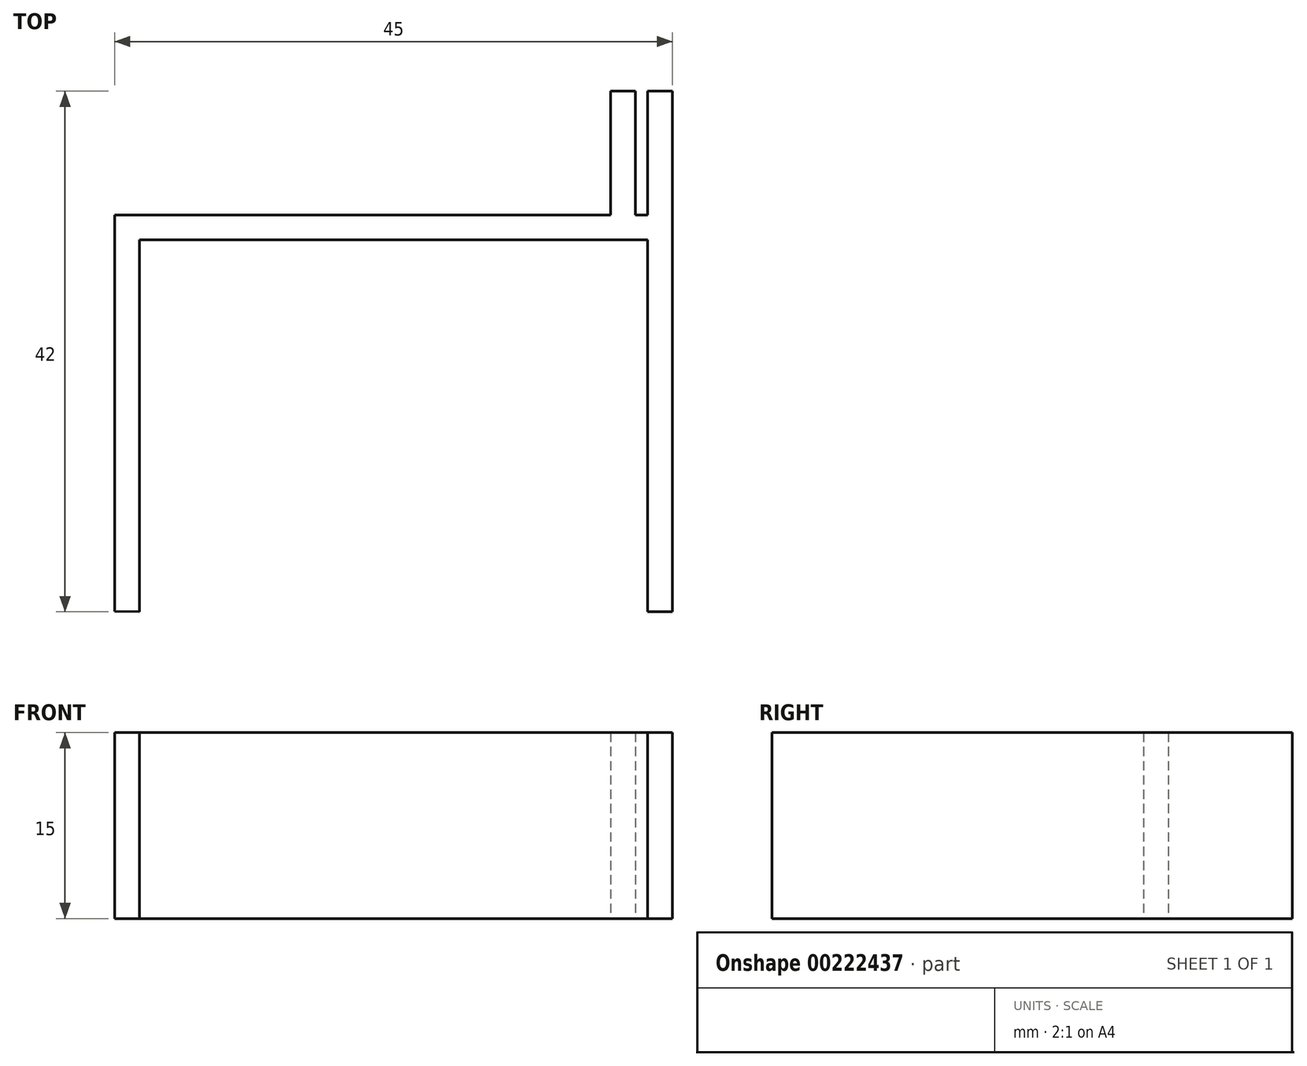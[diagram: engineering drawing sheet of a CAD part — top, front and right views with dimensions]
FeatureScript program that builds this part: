
annotation { "Feature Type Name" : "Feature", "Feature Type Description" : "" }
export const myFeature = defineFeature(function(context is Context, id is Id, definition is map)
    precondition{}
    {
        {
            var Q0;
            Q0=qCreatedBy(makeId("Top.planeOp"),FACE);
            var sketch = newSketch(context, id + "F0", { "sketchPlane" : qUnion([Q0])});
            skLineSegment(sketch, "E0", {"start": v(-24.23, -3.72) * mm, "end": v(16.77, -3.72) * mm});
            skLineSegment(sketch, "E1", {"start": v(-24.23, -3.72) * mm, "end": v(-24.23, -33.72) * mm});
            skLineSegment(sketch, "E2", {"start": v(16.77, -3.72) * mm, "end": v(16.77, -33.72) * mm});
            skLineSegment(sketch, "E3.0", {"start": v(-26.23, -1.72) * mm, "end": v(-26.23, -33.68) * mm});
            skLineSegment(sketch, "E3.1", {"start": v(-26.23, -1.72) * mm, "end": v(18.77, -1.72) * mm});
            skLineSegment(sketch, "E3.2", {"start": v(18.77, -1.72) * mm, "end": v(18.77, -33.72) * mm});
            skLineSegment(sketch, "E4", {"start": v(16.77, -33.72) * mm, "end": v(18.77, -33.72) * mm});
            skLineSegment(sketch, "E5", {"start": v(-24.23, -33.72) * mm, "end": v(-26.23, -33.68) * mm});
            skLineSegment(sketch, "E6.bottom", {"start": v(-26.23, -1.72) * mm, "end": v(-24.23, -1.72) * mm});
            skLineSegment(sketch, "E6.top", {"start": v(-26.23, 8.28) * mm, "end": v(-24.23, 8.28) * mm});
            skLineSegment(sketch, "E6.left", {"start": v(-26.23, -1.72) * mm, "end": v(-26.23, 8.28) * mm});
            skLineSegment(sketch, "E6.right", {"start": v(-24.23, -1.72) * mm, "end": v(-24.23, 8.28) * mm});
            skLineSegment(sketch, "E7", {"start": v(-23.73, -1.72) * mm, "end": v(-23.73, 12.45) * mm, "construction": true});
            skLineSegment(sketch, "E8.MirrorCS", {"start": v(-21.23, -1.72) * mm, "end": v(-23.23, -1.72) * mm});
            skLineSegment(sketch, "E9.MirrorCS", {"start": v(-23.23, -1.72) * mm, "end": v(-23.23, 8.28) * mm});
            skLineSegment(sketch, "E10.MirrorCS", {"start": v(-21.23, -1.72) * mm, "end": v(-21.23, 8.28) * mm});
            skLineSegment(sketch, "E11.MirrorCS", {"start": v(-21.23, 8.28) * mm, "end": v(-23.23, 8.28) * mm});
            skLineSegment(sketch, "E12", {"start": v(-3.73, -1.72) * mm, "end": v(-3.73, 12.19) * mm, "construction": true});
            skLineSegment(sketch, "E13.MirrorCS", {"start": v(13.77, 8.28) * mm, "end": v(15.77, 8.28) * mm});
            skLineSegment(sketch, "E14.MirrorCS", {"start": v(13.77, -1.72) * mm, "end": v(13.77, 8.28) * mm});
            skLineSegment(sketch, "E15.MirrorCS", {"start": v(15.77, -1.72) * mm, "end": v(15.77, 8.28) * mm});
            skLineSegment(sketch, "E16.MirrorCS", {"start": v(16.77, -1.72) * mm, "end": v(16.77, 8.28) * mm});
            skLineSegment(sketch, "E17.MirrorCS", {"start": v(18.77, -1.72) * mm, "end": v(16.77, -1.72) * mm});
            skLineSegment(sketch, "E18.MirrorCS", {"start": v(18.77, 8.28) * mm, "end": v(16.77, 8.28) * mm});
            skLineSegment(sketch, "E19.MirrorCS", {"start": v(18.77, -1.72) * mm, "end": v(18.77, 8.28) * mm});
            skSolve(sketch);
        }
        {
            var Q0;
            Q0=makeQuery(id+"F0.imprint","IMPRINT",FACE,{"disambiguationData":[TD([[makeQuery(id+"F0.imprint","IMPRINT",EDGE,{"derivedFrom":sQuery(id+"F0.wireOp",EDGE,"E0")}),1.0]])]});
            var Q1;
            Q1=makeQuery(id+"F0.imprint","IMPRINT",FACE,{"disambiguationData":[TD([[makeQuery(id+"F0.imprint","IMPRINT",EDGE,{"derivedFrom":sQuery(id+"F0.wireOp",EDGE,"E16.MirrorCS")}),-1.0]])]});
            var Q2;
            Q2=makeQuery(id+"F0.imprint","IMPRINT",FACE,{"disambiguationData":[TD([[makeQuery(id+"F0.imprint","IMPRINT",EDGE,{"derivedFrom":sQuery(id+"F0.wireOp",EDGE,"E8.MirrorCS")}),-1.0]])]});
            var Q3;
            Q3=makeQuery(id+"F0.imprint","IMPRINT",FACE,{"disambiguationData":[TD([[makeQuery(id+"F0.imprint","IMPRINT",EDGE,{"derivedFrom":sQuery(id+"F0.wireOp",EDGE,"E6.bottom")}),1.0]])]});
            var Q4;
            Q4=makeQuery(id+"F0.imprint","IMPRINT",FACE,{"disambiguationData":[TD([[makeQuery(id+"F0.imprint","IMPRINT",EDGE,{"derivedFrom":sQuery(id+"F0.wireOp",EDGE,"E13.MirrorCS")}),-1.0]])]});
            extrude(context, id + "F1", {"entities" : qUnion([Q0, Q1, Q2, Q3, Q4]), "depth" : 15 * mm});
        }
    });
